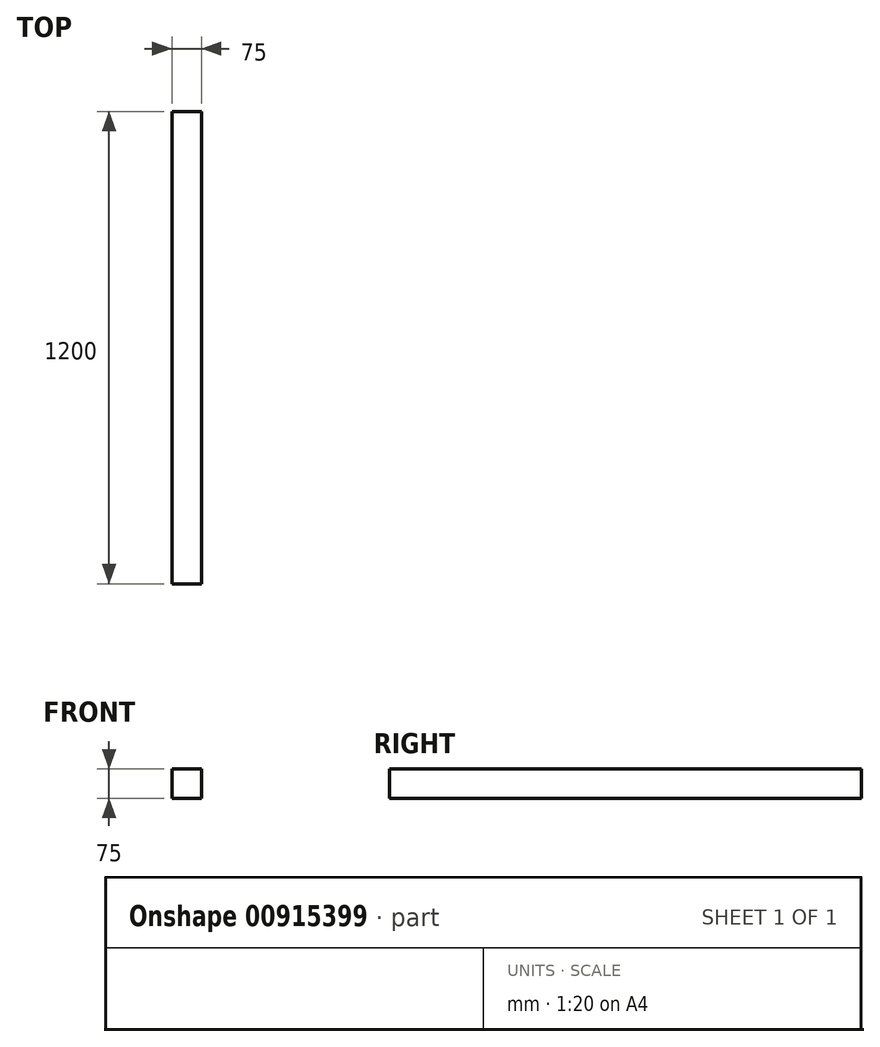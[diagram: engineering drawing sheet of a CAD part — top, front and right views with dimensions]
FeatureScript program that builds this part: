
annotation { "Feature Type Name" : "Feature", "Feature Type Description" : "" }
export const myFeature = defineFeature(function(context is Context, id is Id, definition is map)
    precondition{}
    {
        {
            var Q0;
            Q0=qCreatedBy(makeId("Front.planeOp"),FACE);
            var sketch = newSketch(context, id + "F0", { "sketchPlane" : qUnion([Q0])});
            skLineSegment(sketch, "E0.bottom", {"start": v(-163.08, 7.93) * mm, "end": v(-88.08, 7.93) * mm});
            skLineSegment(sketch, "E0.top", {"start": v(-163.08, -67.07) * mm, "end": v(-88.08, -67.07) * mm});
            skLineSegment(sketch, "E0.left", {"start": v(-163.08, 7.93) * mm, "end": v(-163.08, -67.07) * mm});
            skLineSegment(sketch, "E0.right", {"start": v(-88.08, 7.93) * mm, "end": v(-88.08, -67.07) * mm});
            skSolve(sketch);
        }
        {
            var Q0;
            Q0 = qSketchRegion(id + "F0", true);
            extrude(context, id + "F1", {"entities" : qUnion([Q0]), "depth" : 1200 * mm, "offsetDistance" : 25 * mm});
        }
    });
